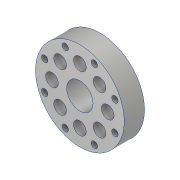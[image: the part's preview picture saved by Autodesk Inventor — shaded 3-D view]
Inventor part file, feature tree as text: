
AUTODESK INVENTOR PART (.ipt)
format: ipt  version: 2020.5 (Build 245400000, 400)  size: 183,296 bytes
history: native  units: mm
features: extrude x4, sketch x4, projected_geometry x1
ambient origin geometry x8: Origin, YZ Plane, XZ Plane, XY Plane, X Axis, Y Axis, Z Axis, Center Point
bodies: Body1 (feature_tree)
feature tree (9):
  extrude  "돌출3"  Depth=10.4mm
  extrude  "돌출4"  Depth=35.0mm
  extrude  "돌출5"  Depth=8.0mm TaperAngle=0.0deg
  extrude  "돌출6"  Depth=22.0mm
  sketch  "스케치3"
  sketch  "스케치4"
  sketch  "스케치5"
  projected_geometry  "투영된 루프2"
  sketch  "스케치6"
